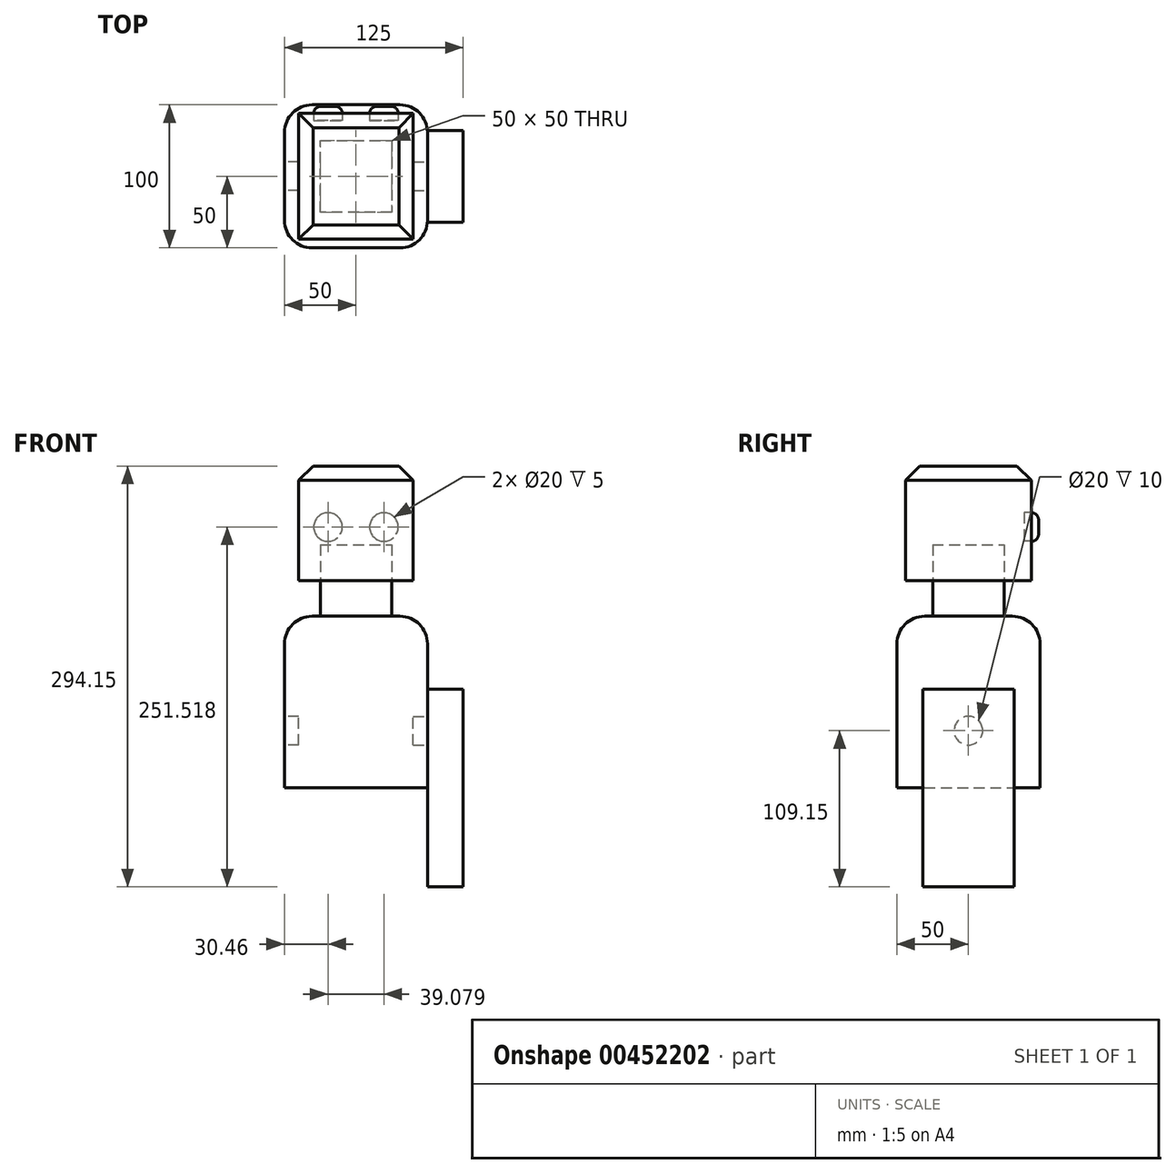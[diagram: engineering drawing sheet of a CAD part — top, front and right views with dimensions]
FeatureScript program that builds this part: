
annotation { "Feature Type Name" : "Feature", "Feature Type Description" : "" }
export const myFeature = defineFeature(function(context is Context, id is Id, definition is map)
    precondition{}
    {
        {
            var Q0;
            Q0=qCreatedBy(makeId("Top.planeOp"),FACE);
            var sketch = newSketch(context, id + "F0", { "sketchPlane" : qUnion([Q0])});
            skCircle(sketch, "E0.cCircle", {"center": v(0, 0) * mm, "radius": 50 * mm, "construction": true});
            skLineSegment(sketch, "E0.0", {"start": v(-50, 50) * mm, "end": v(50, 50) * mm});
            skLineSegment(sketch, "E0.1", {"start": v(50, 50) * mm, "end": v(50, -50) * mm});
            skLineSegment(sketch, "E0.2", {"start": v(50, -50) * mm, "end": v(-50, -50) * mm});
            skLineSegment(sketch, "E0.3", {"start": v(-50, -50) * mm, "end": v(-50, 50) * mm});
            skPoint(sketch, "E0.0.midPoint", {"position": v(0, 50) * mm});
            skSolve(sketch);
        }
        {
            var Q0;
            Q0=makeQuery(id+"F0.imprint","IMPRINT",FACE,{"disambiguationData":[TD([[makeQuery(id+"F0.imprint","IMPRINT",EDGE,{"derivedFrom":sQuery(id+"F0.wireOp",EDGE,"E0.0")}),-1.0]])]});
            extrude(context, id + "F1", {"entities" : qUnion([Q0]), "depth" : 120 * mm});
        }
        {
            var Q0;
            Q0=makeQuery(id+"F1.opExtrude","CAP_FACE",FACE,{"disambiguationData":[OSD([sQuery(id+"F0.wireOp",EDGE,"E0.0"),sQuery(id+"F0.wireOp",EDGE,"E0.1"),sQuery(id+"F0.wireOp",EDGE,"E0.2"),sQuery(id+"F0.wireOp",EDGE,"E0.3")])],"isStart":false});
            var sketch = newSketch(context, id + "F2", { "sketchPlane" : qUnion([Q0])});
            skCircle(sketch, "E1.cCircle", {"center": v(0, 0) * mm, "radius": 25 * mm, "construction": true});
            skLineSegment(sketch, "E1.0", {"start": v(-25, 25) * mm, "end": v(25, 25) * mm});
            skLineSegment(sketch, "E1.1", {"start": v(25, 25) * mm, "end": v(25, -25) * mm});
            skLineSegment(sketch, "E1.2", {"start": v(25, -25) * mm, "end": v(-25, -25) * mm});
            skLineSegment(sketch, "E1.3", {"start": v(-25, -25) * mm, "end": v(-25, 25) * mm});
            skPoint(sketch, "E1.0.midPoint", {"position": v(0, 25) * mm});
            skSolve(sketch);
        }
        {
            var Q0;
            Q0=makeQuery(id+"F2.imprint","IMPRINT",FACE,{"disambiguationData":[TD([[makeQuery(id+"F2.imprint","IMPRINT",EDGE,{"derivedFrom":sQuery(id+"F2.wireOp",EDGE,"E1.0")}),-1.0]])]});
            extrude(context, id + "F3", {"entities" : qUnion([Q0]), "operationType" : NewBodyOperationType.ADD, "depth" : 50 * mm});
        }
        {
            var Q0;
            Q0=qCreatedBy(makeId("Top.planeOp"),FACE);
            cPlane(context, id + "F4", {"entities" : qUnion([Q0]), "cplaneType" : CPlaneType.OFFSET, "offset" : 145 * mm, "width" : 150 * mm, "height" : 150 * mm});
        }
        {
            var Q0;
            Q0=qCreatedBy(id+"F4.planeOp",FACE);
            var sketch = newSketch(context, id + "F5", { "sketchPlane" : qUnion([Q0])});
            skLineSegment(sketch, "E2.bottom", {"start": v(40, 43.97) * mm, "end": v(-40, 43.97) * mm});
            skLineSegment(sketch, "E2.top", {"start": v(40, -43.97) * mm, "end": v(-40, -43.97) * mm});
            skLineSegment(sketch, "E2.left", {"start": v(40, 43.97) * mm, "end": v(40, -43.97) * mm});
            skLineSegment(sketch, "E2.right", {"start": v(-40, 43.97) * mm, "end": v(-40, -43.97) * mm});
            skPoint(sketch, "E2.middle", {"position": v(0, 0) * mm});
            skSolve(sketch);
        }
        {
            var Q0;
            Q0=makeQuery(id+"F5.imprint","IMPRINT",FACE,{"disambiguationData":[TD([[makeQuery(id+"F5.imprint","IMPRINT",EDGE,{"derivedFrom":sQuery(id+"F5.wireOp",EDGE,"E2.bottom")}),1.0]])]});
            extrude(context, id + "F6", {"entities" : qUnion([Q0]), "depth" : 80 * mm});
        }
        {
            var Q0;
            Q0=makeQuery(id+"F1.opExtrude","SWEPT_BODY",BODY,{"disambiguationData":[OSD([sQuery(id+"F0.wireOp",EDGE,"E0.0"),sQuery(id+"F0.wireOp",EDGE,"E0.1"),sQuery(id+"F0.wireOp",EDGE,"E0.2"),sQuery(id+"F0.wireOp",EDGE,"E0.3")])]});
            var Q1;
            Q1=makeQuery(id+"F6.opExtrude","SWEPT_BODY",BODY,{"disambiguationData":[OSD([sQuery(id+"F5.wireOp",EDGE,"E2.bottom"),sQuery(id+"F5.wireOp",EDGE,"E2.top"),sQuery(id+"F5.wireOp",EDGE,"E2.left"),sQuery(id+"F5.wireOp",EDGE,"E2.right")])]});
            booleanBodies(context, id + "F7", {"operationType" : BooleanOperationType.SUBTRACTION, "tools" : qUnion([Q0]), "targets" : qUnion([Q1]), "keepTools" : true});
        }
        {
            var Q0;
            Q0=makeQuery(id+"F1.opExtrude","SWEPT_FACE",FACE,{"disambiguationData":[OSD([sQuery(id+"F0.wireOp",EDGE,"E0.1")])]});
            var sketch = newSketch(context, id + "F8", { "sketchPlane" : qUnion([Q0])});
            skLineSegment(sketch, "E3", {"start": v(0, 0) * mm, "end": v(0, 40) * mm});
            skPoint(sketch, "E3.endSnap0", {"position": v(0, 0) * mm});
            skCircle(sketch, "E4", {"center": v(0, 40) * mm, "radius": 10 * mm});
            skSolve(sketch);
        }
        {
            var Q0;
            Q0=makeQuery(id+"F8.imprint","IMPRINT",FACE,{"disambiguationData":[TD([[makeQuery(id+"F8.imprint","IMPRINT",EDGE,{"derivedFrom":sQuery(id+"F8.wireOp",EDGE,"E4")}),1.0]])]});
            extrude(context, id + "F9", {"entities" : qUnion([Q0]), "oppositeDirection" : true, "depth" : 10 * mm});
        }
        {
            var Q0;
            Q0=makeQuery(id+"F1.opExtrude","SWEPT_FACE",FACE,{"disambiguationData":[OSD([sQuery(id+"F0.wireOp",EDGE,"E0.1")])]});
            var sketch = newSketch(context, id + "F10", { "sketchPlane" : qUnion([Q0])});
            skLineSegment(sketch, "E5.bottom", {"start": v(31.98, 69.15) * mm, "end": v(-31.98, 69.15) * mm});
            skLineSegment(sketch, "E5.top", {"start": v(31.98, -69.15) * mm, "end": v(-31.98, -69.15) * mm});
            skLineSegment(sketch, "E5.left", {"start": v(31.98, 69.15) * mm, "end": v(31.98, -69.15) * mm});
            skLineSegment(sketch, "E5.right", {"start": v(-31.98, 69.15) * mm, "end": v(-31.98, -69.15) * mm});
            skPoint(sketch, "E5.middle", {"position": v(0, 0) * mm});
            skSolve(sketch);
        }
        {
            var Q0;
            {var subQ0=sQuery(id+"F10.wireOp",EDGE,"E5.top");Q0=makeQuery(id+"F10.imprint","IMPRINT",FACE,{"disambiguationData":[TD([[makeQuery(id+"F10.imprint","IMPRINT",EDGE,{"derivedFrom":subQ0}),-1.0]])]});}
            var Q1;
            {var subQ0=sQuery(id+"F10.wireOp",EDGE,"E5.bottom");Q1=makeQuery(id+"F10.imprint","IMPRINT",FACE,{"disambiguationData":[TD([[makeQuery(id+"F10.imprint","IMPRINT",EDGE,{"derivedFrom":subQ0}),1.0]])]});}
            extrude(context, id + "F11", {"entities" : qUnion([Q0, Q1]), "depth" : 25 * mm});
        }
        {
            var Q0;
            Q0=makeQuery(id+"F9.opExtrude","SWEPT_BODY",BODY,{"disambiguationData":[OSD([sQuery(id+"F8.wireOp",EDGE,"E4")])]});
            var Q1;
            Q1=makeQuery(id+"F1.opExtrude","SWEPT_BODY",BODY,{"disambiguationData":[OSD([sQuery(id+"F0.wireOp",EDGE,"E0.0"),sQuery(id+"F0.wireOp",EDGE,"E0.1"),sQuery(id+"F0.wireOp",EDGE,"E0.2"),sQuery(id+"F0.wireOp",EDGE,"E0.3")])]});
            booleanBodies(context, id + "F12", {"operationType" : BooleanOperationType.SUBTRACTION, "tools" : qUnion([Q0]), "targets" : qUnion([Q1]), "keepTools" : true});
        }
        {
            var Q0;
            Q0=makeQuery(id+"F9.opExtrude","SWEPT_BODY",BODY,{"disambiguationData":[OSD([sQuery(id+"F8.wireOp",EDGE,"E4")])]});
            var Q1;
            Q1=qCreatedBy(makeId("Right.planeOp"),FACE);
            mirror(context, id + "F13", {"entities" : qUnion([Q0]), "mirrorPlane" : qUnion([Q1])});
        }
        {
            var Q0;
            Q0=makeQuery(id+"F1.opExtrude","CAP_EDGE",EDGE,{"disambiguationData":[OSD([sQuery(id+"F0.wireOp",EDGE,"E0.2")])],"isStart":false});
            var Q1;
            Q1=makeQuery(id+"F1.opExtrude","SWEPT_EDGE",EDGE,{"disambiguationData":[OSD([sQuery(id+"F0.wireOp",EDGE,"E0.2"),sQuery(id+"F0.wireOp",EDGE,"E0.3")])]});
            var Q2;
            Q2=makeQuery(id+"F1.opExtrude","SWEPT_EDGE",EDGE,{"disambiguationData":[OSD([sQuery(id+"F0.wireOp",EDGE,"E0.1"),sQuery(id+"F0.wireOp",EDGE,"E0.2")])]});
            var Q3;
            Q3=makeQuery(id+"F1.opExtrude","SWEPT_EDGE",EDGE,{"disambiguationData":[OSD([sQuery(id+"F0.wireOp",EDGE,"E0.0"),sQuery(id+"F0.wireOp",EDGE,"E0.1")])]});
            var Q4;
            Q4=makeQuery(id+"F1.opExtrude","CAP_EDGE",EDGE,{"disambiguationData":[OSD([sQuery(id+"F0.wireOp",EDGE,"E0.0")])],"isStart":false});
            var Q5;
            Q5=makeQuery(id+"F1.opExtrude","CAP_EDGE",EDGE,{"disambiguationData":[OSD([sQuery(id+"F0.wireOp",EDGE,"E0.1")])],"isStart":false});
            var Q6;
            Q6=makeQuery(id+"F1.opExtrude","SWEPT_EDGE",EDGE,{"disambiguationData":[OSD([sQuery(id+"F0.wireOp",EDGE,"E0.0"),sQuery(id+"F0.wireOp",EDGE,"E0.3")])]});
            var Q7;
            Q7=makeQuery(id+"F1.opExtrude","CAP_EDGE",EDGE,{"disambiguationData":[OSD([sQuery(id+"F0.wireOp",EDGE,"E0.3")])],"isStart":false});
            fillet(context, id + "F14", {"entities" : qUnion([Q0, Q1, Q2, Q3, Q4, Q5, Q6, Q7]), "radius" : 19.3 * mm, "tangentPropagation" : true, "allowEdgeOverflow" : false});
        }
        {
            var Q0;
            Q0=makeQuery(id+"F6.opExtrude","CAP_EDGE",EDGE,{"disambiguationData":[OSD([sQuery(id+"F5.wireOp",EDGE,"E2.right")])],"isStart":false});
            var Q1;
            Q1=makeQuery(id+"F6.opExtrude","CAP_EDGE",EDGE,{"disambiguationData":[OSD([sQuery(id+"F5.wireOp",EDGE,"E2.bottom")])],"isStart":false});
            var Q2;
            Q2=makeQuery(id+"F6.opExtrude","CAP_EDGE",EDGE,{"disambiguationData":[OSD([sQuery(id+"F5.wireOp",EDGE,"E2.left")])],"isStart":false});
            var Q3;
            Q3=makeQuery(id+"F6.opExtrude","CAP_EDGE",EDGE,{"disambiguationData":[OSD([sQuery(id+"F5.wireOp",EDGE,"E2.top")])],"isStart":false});
            chamfer(context, id + "F15", {"entities" : qUnion([Q0, Q1, Q2, Q3]), "width" : 10 * mm, "tangentPropagation" : true});
        }
        {
            var Q0;
            Q0=makeQuery(id+"F6.opExtrude","SWEPT_FACE",FACE,{"disambiguationData":[OSD([sQuery(id+"F5.wireOp",EDGE,"E2.bottom")])]});
            var sketch = newSketch(context, id + "F16", { "sketchPlane" : qUnion([Q0])});
            skCircle(sketch, "E6", {"center": v(-19.54, 182.37) * mm, "radius": 10 * mm});
            skSolve(sketch);
        }
        {
            var Q0;
            Q0=makeQuery(id+"F16.imprint","IMPRINT",FACE,{"disambiguationData":[TD([[makeQuery(id+"F16.imprint","IMPRINT",EDGE,{"derivedFrom":sQuery(id+"F16.wireOp",EDGE,"E6")}),1.0]])]});
            extrude(context, id + "F17", {"entities" : qUnion([Q0]), "endBound" : BoundingType.SYMMETRIC, "depth" : 10 * mm});
        }
        {
            var Q0;
            Q0=makeQuery(id+"F17.opExtrude","SWEPT_BODY",BODY,{"disambiguationData":[OSD([sQuery(id+"F16.wireOp",EDGE,"E6")])]});
            var Q1;
            Q1=qCreatedBy(makeId("Right.planeOp"),FACE);
            mirror(context, id + "F18", {"entities" : qUnion([Q0]), "mirrorPlane" : qUnion([Q1])});
        }
        {
            var Q0;
            Q0=makeQuery(id+"F17.opExtrude","SWEPT_BODY",BODY,{"disambiguationData":[OSD([sQuery(id+"F16.wireOp",EDGE,"E6")])]});
            var Q1;
            Q1=makeQuery(id+"F18.opPattern","COPY",BODY,{"derivedFrom":makeQuery(id+"F17.opExtrude","SWEPT_BODY",BODY,{"disambiguationData":[OSD([sQuery(id+"F16.wireOp",EDGE,"E6")])]}),"instanceName":"1"});
            var Q2;
            Q2=makeQuery(id+"F6.opExtrude","SWEPT_BODY",BODY,{"disambiguationData":[OSD([sQuery(id+"F5.wireOp",EDGE,"E2.bottom"),sQuery(id+"F5.wireOp",EDGE,"E2.top"),sQuery(id+"F5.wireOp",EDGE,"E2.left"),sQuery(id+"F5.wireOp",EDGE,"E2.right")])]});
            booleanBodies(context, id + "F19", {"operationType" : BooleanOperationType.SUBTRACTION, "tools" : qUnion([Q0, Q1]), "targets" : qUnion([Q2]), "keepTools" : true});
        }
        {
            var Q0;
            Q0=makeQuery(id+"F17.opExtrude","CAP_FACE",FACE,{"disambiguationData":[OSD([sQuery(id+"F16.wireOp",EDGE,"E6")])],"isStart":false});
            var Q1;
            Q1=makeQuery(id+"F18.opPattern","COPY",EDGE,{"derivedFrom":makeQuery(id+"F17.opExtrude","CAP_EDGE",EDGE,{"disambiguationData":[OSD([sQuery(id+"F16.wireOp",EDGE,"E6")])],"isStart":false}),"instanceName":"1"});
            fillet(context, id + "F20", {"entities" : qUnion([Q0, Q1]), "radius" : 5 * mm, "tangentPropagation" : true, "allowEdgeOverflow" : false});
        }
    });
